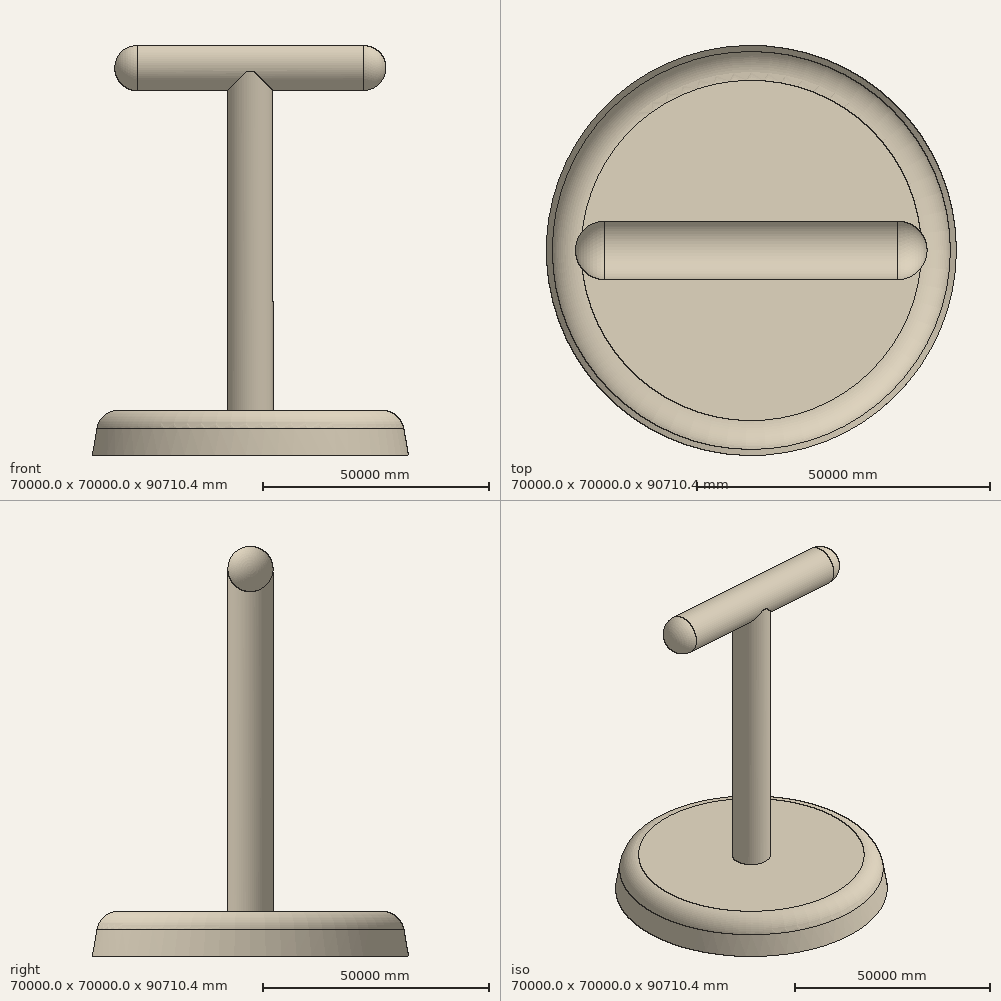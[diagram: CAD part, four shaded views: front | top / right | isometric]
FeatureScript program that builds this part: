
annotation { "Feature Type Name" : "Feature", "Feature Type Description" : "" }
export const myFeature = defineFeature(function(context is Context, id is Id, definition is map)
    precondition{}
    {
        {
            var Q0;
            Q0=qCreatedBy(makeId("Top.planeOp"),FACE);
            var sketch = newSketch(context, id + "F0", { "sketchPlane" : qUnion([Q0])});
            skCircle(sketch, "E0", {"center": v(0, 0) * mm, "radius": 35000 * mm});
            skSolve(sketch);
        }
        {
            var Q0;
            Q0 = qSketchRegion(id + "F0", true);
            extrude(context, id + "F1", {"entities" : qUnion([Q0]), "depth" : 10000 * mm, "hasDraft" : true, "draftAngle" : 10 * degree, "draftPullDirection" : true});
        }
        {
            var Q0;
            Q0=makeQuery(id+"F1.opExtrude","CAP_FACE",FACE,{"disambiguationData":[OSD([sQuery(id+"F0.wireOp",EDGE,"E0")])],"isStart":false});
            var sketch = newSketch(context, id + "F2", { "sketchPlane" : qUnion([Q0])});
            skCircle(sketch, "E1", {"center": v(0, 0) * mm, "radius": 5000 * mm});
            skSolve(sketch);
        }
        {
            var Q0;
            Q0 = qSketchRegion(id + "F2", true);
            extrude(context, id + "F3", {"entities" : qUnion([Q0]), "operationType" : NewBodyOperationType.ADD, "depth" : 75000 * mm});
        }
        {
            var Q0;
            Q0=qCreatedBy(makeId("Right.planeOp"),FACE);
            var sketch = newSketch(context, id + "F4", { "sketchPlane" : qUnion([Q0])});
            skCircle(sketch, "E2", {"center": v(0, 85710.37) * mm, "radius": 5000 * mm});
            skSolve(sketch);
        }
        {
            var Q0;
            Q0 = qSketchRegion(id + "F4", true);
            extrude(context, id + "F5", {"entities" : qUnion([Q0]), "operationType" : NewBodyOperationType.ADD, "depth" : 30000 * mm, "hasSecondDirection" : true, "secondDirectionOppositeDirection" : true, "secondDirectionDepth" : 30000 * mm});
        }
        {
            var Q0;
            Q0=makeQuery(id+"F5.opExtrude","CAP_EDGE",EDGE,{"disambiguationData":[OSD([sQuery(id+"F4.wireOp",EDGE,"E2")])],"isStart":false});
            var Q1;
            Q1=makeQuery(id+"F5.opExtrude","CAP_EDGE",EDGE,{"disambiguationData":[OSD([sQuery(id+"F4.wireOp",EDGE,"E2")])],"isStart":true});
            fillet(context, id + "F6", {"entities" : qUnion([Q0, Q1]), "radius" : 5000 * mm, "tangentPropagation" : true, "allowEdgeOverflow" : false});
        }
        {
            var Q0;
            Q0=makeQuery(id+"F1.opExtrude","CAP_EDGE",EDGE,{"disambiguationData":[OSD([sQuery(id+"F0.wireOp",EDGE,"E0")])],"isStart":false});
            fillet(context, id + "F7", {"entities" : qUnion([Q0]), "radius" : 5000 * mm, "tangentPropagation" : true, "allowEdgeOverflow" : false});
        }
    });
